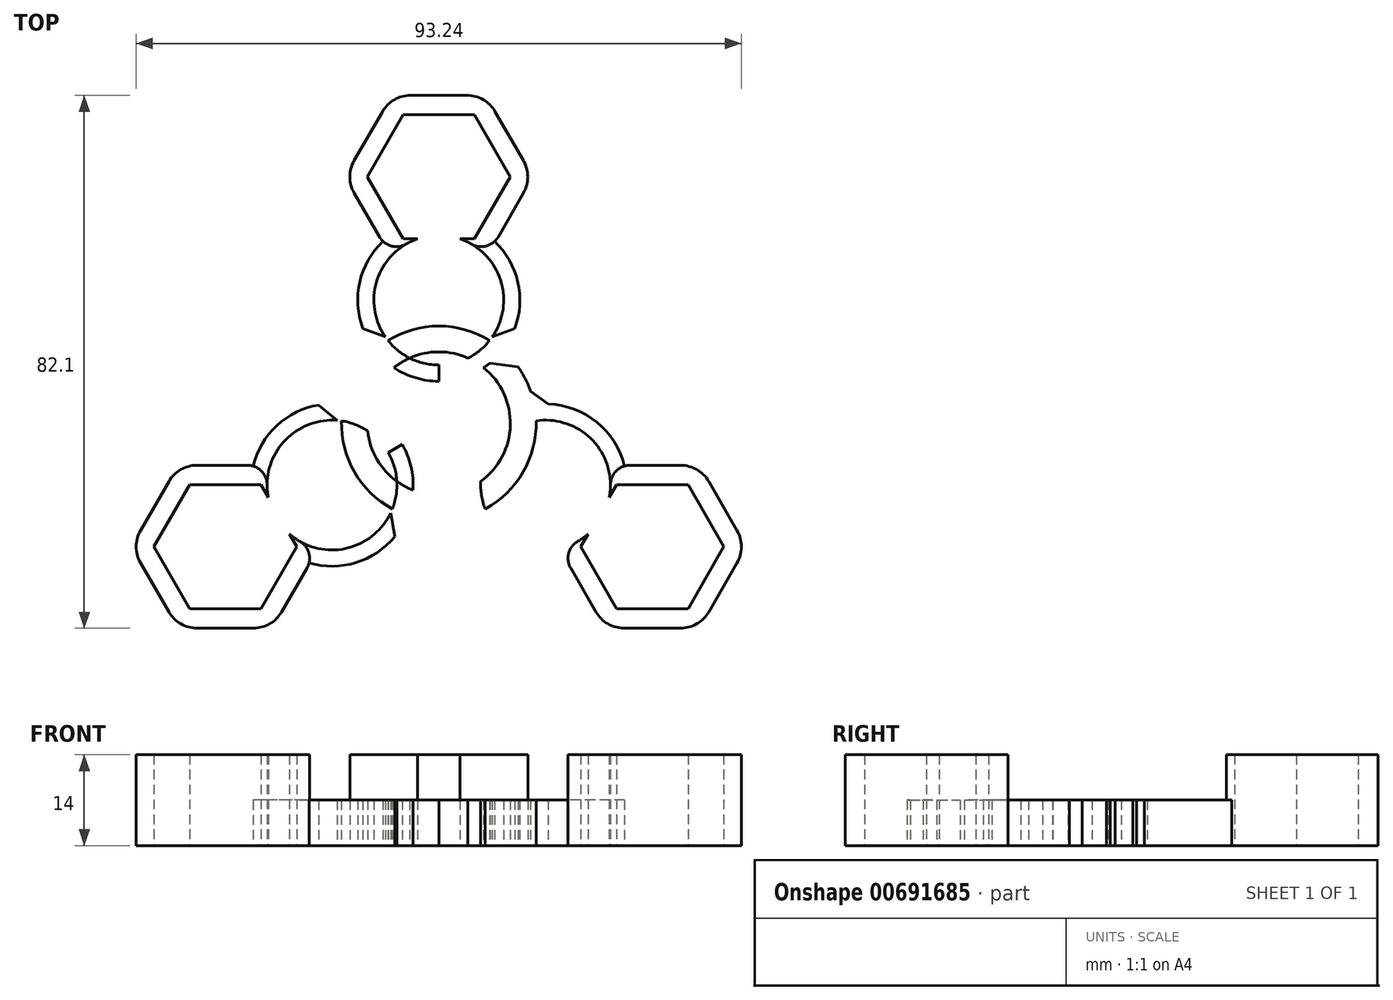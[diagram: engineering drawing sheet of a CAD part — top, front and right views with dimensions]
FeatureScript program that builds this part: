
annotation { "Feature Type Name" : "Feature", "Feature Type Description" : "" }
export const myFeature = defineFeature(function(context is Context, id is Id, definition is map)
    precondition{}
    {
        {
            var Q0;
            Q0=qCreatedBy(makeId("Top.planeOp"),FACE);
            var sketch = newSketch(context, id + "F0", { "sketchPlane" : qUnion([Q0])});
            skCircle(sketch, "E0", {"center": v(0, 0) * mm, "radius": 11.03 * mm});
            skCircle(sketch, "E1", {"center": v(0, 0) * mm, "radius": 15 * mm});
            skLineSegment(sketch, "E2", {"start": v(0, 0) * mm, "end": v(0, 38) * mm});
            skCircle(sketch, "E3.cCircle", {"center": v(0, 38) * mm, "radius": 11.03 * mm, "construction": true});
            skLineSegment(sketch, "E3.0", {"start": v(11.02, 38) * mm, "end": v(5.51, 28.45) * mm});
            skLineSegment(sketch, "E3.1", {"start": v(5.51, 28.45) * mm, "end": v(-5.51, 28.45) * mm});
            skLineSegment(sketch, "E3.2", {"start": v(-5.51, 28.45) * mm, "end": v(-11.02, 38) * mm});
            skLineSegment(sketch, "E3.3", {"start": v(-11.02, 38) * mm, "end": v(-5.51, 47.55) * mm});
            skLineSegment(sketch, "E3.4", {"start": v(-5.51, 47.55) * mm, "end": v(5.51, 47.55) * mm});
            skLineSegment(sketch, "E3.5", {"start": v(5.51, 47.55) * mm, "end": v(11.02, 38) * mm});
            skCircle(sketch, "E4", {"center": v(0, 19) * mm, "radius": 10 * mm});
            skCircle(sketch, "E5", {"center": v(0, 19) * mm, "radius": 12.5 * mm});
            skCircle(sketch, "E6.cCircle", {"center": v(0, 38) * mm, "radius": 14.49 * mm, "construction": true});
            skLineSegment(sketch, "E6.0", {"start": v(7.24, 25.45) * mm, "end": v(-7.24, 25.45) * mm});
            skLineSegment(sketch, "E6.1", {"start": v(-7.24, 25.45) * mm, "end": v(-14.49, 38) * mm});
            skLineSegment(sketch, "E6.2", {"start": v(-14.49, 38) * mm, "end": v(-7.24, 50.55) * mm});
            skLineSegment(sketch, "E6.3", {"start": v(-7.24, 50.55) * mm, "end": v(7.24, 50.55) * mm});
            skLineSegment(sketch, "E6.4", {"start": v(7.24, 50.55) * mm, "end": v(14.49, 38) * mm});
            skLineSegment(sketch, "E6.5", {"start": v(14.49, 38) * mm, "end": v(7.24, 25.45) * mm});
            skLineSegment(sketch, "E7.1.1", {"start": v(-25.66, -31.55) * mm, "end": v(-40.15, -31.55) * mm});
            skLineSegment(sketch, "E7.1.2", {"start": v(-18.42, -19) * mm, "end": v(-25.66, -31.55) * mm});
            skLineSegment(sketch, "E7.1.3", {"start": v(-47.4, -19) * mm, "end": v(-40.15, -6.45) * mm});
            skLineSegment(sketch, "E7.1.4", {"start": v(-25.66, -6.45) * mm, "end": v(-18.42, -19) * mm});
            skLineSegment(sketch, "E7.1.5", {"start": v(-40.15, -31.55) * mm, "end": v(-47.4, -19) * mm});
            skLineSegment(sketch, "E7.1.7", {"start": v(0, 0) * mm, "end": v(-32.9, -19) * mm});
            skCircle(sketch, "E7.1.8", {"center": v(-32.9, -19) * mm, "radius": 11.03 * mm, "construction": true});
            skLineSegment(sketch, "E7.1.9", {"start": v(-38.42, -9.45) * mm, "end": v(-27.4, -9.45) * mm});
            skLineSegment(sketch, "E7.1.10", {"start": v(-27.4, -9.45) * mm, "end": v(-21.88, -19) * mm});
            skLineSegment(sketch, "E7.1.11", {"start": v(-21.88, -19) * mm, "end": v(-27.4, -28.55) * mm});
            skCircle(sketch, "E7.1.12", {"center": v(-32.9, -19) * mm, "radius": 14.49 * mm, "construction": true});
            skCircle(sketch, "E7.1.13", {"center": v(-16.45, -9.5) * mm, "radius": 10 * mm});
            skLineSegment(sketch, "E7.1.14", {"start": v(-27.4, -28.55) * mm, "end": v(-38.42, -28.55) * mm});
            skLineSegment(sketch, "E7.1.15", {"start": v(-38.42, -28.55) * mm, "end": v(-43.93, -19) * mm});
            skLineSegment(sketch, "E7.1.16", {"start": v(-43.93, -19) * mm, "end": v(-38.42, -9.45) * mm});
            skCircle(sketch, "E7.1.17", {"center": v(-16.45, -9.5) * mm, "radius": 12.5 * mm});
            skLineSegment(sketch, "E7.1.18", {"start": v(-40.15, -6.45) * mm, "end": v(-25.66, -6.45) * mm});
            skLineSegment(sketch, "E7.2.1", {"start": v(40.15, -6.45) * mm, "end": v(47.4, -19) * mm});
            skLineSegment(sketch, "E7.2.2", {"start": v(25.66, -6.45) * mm, "end": v(40.15, -6.45) * mm});
            skLineSegment(sketch, "E7.2.3", {"start": v(40.15, -31.55) * mm, "end": v(25.66, -31.55) * mm});
            skLineSegment(sketch, "E7.2.4", {"start": v(18.42, -19) * mm, "end": v(25.66, -6.45) * mm});
            skLineSegment(sketch, "E7.2.5", {"start": v(47.4, -19) * mm, "end": v(40.15, -31.55) * mm});
            skLineSegment(sketch, "E7.2.7", {"start": v(0, 0) * mm, "end": v(32.9, -19) * mm});
            skCircle(sketch, "E7.2.8", {"center": v(32.9, -19) * mm, "radius": 11.03 * mm, "construction": true});
            skLineSegment(sketch, "E7.2.9", {"start": v(27.4, -28.55) * mm, "end": v(21.88, -19) * mm});
            skLineSegment(sketch, "E7.2.10", {"start": v(21.88, -19) * mm, "end": v(27.4, -9.45) * mm});
            skLineSegment(sketch, "E7.2.11", {"start": v(27.4, -9.45) * mm, "end": v(38.42, -9.45) * mm});
            skCircle(sketch, "E7.2.12", {"center": v(32.9, -19) * mm, "radius": 14.49 * mm, "construction": true});
            skCircle(sketch, "E7.2.13", {"center": v(16.45, -9.5) * mm, "radius": 10 * mm});
            skLineSegment(sketch, "E7.2.14", {"start": v(38.42, -9.45) * mm, "end": v(43.93, -19) * mm});
            skLineSegment(sketch, "E7.2.15", {"start": v(43.93, -19) * mm, "end": v(38.42, -28.55) * mm});
            skLineSegment(sketch, "E7.2.16", {"start": v(38.42, -28.55) * mm, "end": v(27.4, -28.55) * mm});
            skCircle(sketch, "E7.2.17", {"center": v(16.45, -9.5) * mm, "radius": 12.5 * mm});
            skLineSegment(sketch, "E7.2.18", {"start": v(25.66, -31.55) * mm, "end": v(18.42, -19) * mm});
            skSolve(sketch);
        }
        {
            var Q0;
            {var subQ0=sQuery(id+"F0.wireOp",EDGE,"E0");var subQ1=sQuery(id+"F0.wireOp",EDGE,"E7.1.13");var subQ2=makeQuery(id+"F0.imprint","INTERSECT",VERTEX,{"disambiguationData":[OD(1.0)],"derivedFrom":[subQ1,subQ0]});Q0=makeQuery(id+"F0.imprint","IMPRINT",FACE,{"disambiguationData":[TD([[makeQuery(id+"F0.imprint","IMPRINT",EDGE,{"disambiguationData":[TD([[subQ2,-1.0]])],"derivedFrom":subQ1}),-1.0]])]});}
            var Q1;
            {var subQ0=sQuery(id+"F0.wireOp",EDGE,"E1");var subQ1=sQuery(id+"F0.wireOp",EDGE,"E5");var subQ2=makeQuery(id+"F0.imprint","INTERSECT",VERTEX,{"disambiguationData":[OD(0.0)],"derivedFrom":[subQ1,subQ0]});Q1=makeQuery(id+"F0.imprint","IMPRINT",FACE,{"disambiguationData":[TD([[makeQuery(id+"F0.imprint","IMPRINT",EDGE,{"disambiguationData":[TD([[subQ2,-1.0]])],"derivedFrom":subQ1}),-1.0]])]});}
            var Q2;
            {var subQ0=sQuery(id+"F0.wireOp",EDGE,"E1");var subQ1=sQuery(id+"F0.wireOp",EDGE,"E4");var subQ2=makeQuery(id+"F0.imprint","INTERSECT",VERTEX,{"disambiguationData":[OD(0.0)],"derivedFrom":[subQ1,subQ0]});Q2=makeQuery(id+"F0.imprint","IMPRINT",FACE,{"disambiguationData":[TD([[makeQuery(id+"F0.imprint","IMPRINT",EDGE,{"disambiguationData":[TD([[subQ2,-1.0]])],"derivedFrom":subQ1}),-1.0]])]});}
            var Q3;
            {var subQ0=sQuery(id+"F0.wireOp",EDGE,"E0");var subQ1=sQuery(id+"F0.wireOp",EDGE,"E4");var subQ2=makeQuery(id+"F0.imprint","INTERSECT",VERTEX,{"disambiguationData":[OD(1.0)],"derivedFrom":[subQ1,subQ0]});Q3=makeQuery(id+"F0.imprint","IMPRINT",FACE,{"disambiguationData":[TD([[makeQuery(id+"F0.imprint","IMPRINT",EDGE,{"disambiguationData":[TD([[subQ2,-1.0]])],"derivedFrom":subQ1}),-1.0]])]});}
            var Q4;
            {var subQ0=sQuery(id+"F0.wireOp",EDGE,"E1");var subQ1=sQuery(id+"F0.wireOp",EDGE,"E5");var subQ2=makeQuery(id+"F0.imprint","INTERSECT",VERTEX,{"disambiguationData":[OD(1.0)],"derivedFrom":[subQ1,subQ0]});Q4=makeQuery(id+"F0.imprint","IMPRINT",FACE,{"disambiguationData":[TD([[makeQuery(id+"F0.imprint","IMPRINT",EDGE,{"disambiguationData":[TD([[subQ2,1.0]])],"derivedFrom":subQ1}),-1.0]])]});}
            var Q5;
            {var subQ0=sQuery(id+"F0.wireOp",EDGE,"E7.2.13");var subQ1=sQuery(id+"F0.wireOp",EDGE,"E0");var subQ2=makeQuery(id+"F0.imprint","INTERSECT",VERTEX,{"disambiguationData":[OD(1.0)],"derivedFrom":[subQ1,subQ0]});Q5=makeQuery(id+"F0.imprint","IMPRINT",FACE,{"disambiguationData":[TD([[makeQuery(id+"F0.imprint","IMPRINT",EDGE,{"disambiguationData":[TD([[subQ2,-1.0]])],"derivedFrom":subQ1}),-1.0]])]});}
            var Q6;
            {var subQ0=sQuery(id+"F0.wireOp",EDGE,"E7.2.17");var subQ1=sQuery(id+"F0.wireOp",EDGE,"E0");var subQ2=makeQuery(id+"F0.imprint","INTERSECT",VERTEX,{"disambiguationData":[OD(0.0)],"derivedFrom":[subQ1,subQ0]});Q6=makeQuery(id+"F0.imprint","IMPRINT",FACE,{"disambiguationData":[TD([[makeQuery(id+"F0.imprint","IMPRINT",EDGE,{"disambiguationData":[TD([[subQ2,-1.0]])],"derivedFrom":subQ1}),-1.0]])]});}
            var Q7;
            {var subQ0=sQuery(id+"F0.wireOp",EDGE,"E1");var subQ1=sQuery(id+"F0.wireOp",EDGE,"E7.1.17");var subQ2=makeQuery(id+"F0.imprint","INTERSECT",VERTEX,{"disambiguationData":[OD(0.0)],"derivedFrom":[subQ1,subQ0]});Q7=makeQuery(id+"F0.imprint","IMPRINT",FACE,{"disambiguationData":[TD([[makeQuery(id+"F0.imprint","IMPRINT",EDGE,{"disambiguationData":[TD([[subQ2,-1.0]])],"derivedFrom":subQ1}),-1.0]])]});}
            var Q8;
            {var subQ0=sQuery(id+"F0.wireOp",EDGE,"E1");var subQ1=sQuery(id+"F0.wireOp",EDGE,"E7.1.13");var subQ2=makeQuery(id+"F0.imprint","INTERSECT",VERTEX,{"disambiguationData":[OD(0.0)],"derivedFrom":[subQ1,subQ0]});Q8=makeQuery(id+"F0.imprint","IMPRINT",FACE,{"disambiguationData":[TD([[makeQuery(id+"F0.imprint","IMPRINT",EDGE,{"disambiguationData":[TD([[subQ2,-1.0]])],"derivedFrom":subQ1}),-1.0]])]});}
            var Q9;
            {var subQ0=sQuery(id+"F0.wireOp",EDGE,"E7.1.18");var subQ1=sQuery(id+"F0.wireOp",EDGE,"E7.1.13");var subQ2=makeQuery(id+"F0.imprint","INTERSECT",VERTEX,{"derivedFrom":[subQ1,subQ0]});Q9=makeQuery(id+"F0.imprint","IMPRINT",FACE,{"disambiguationData":[TD([[makeQuery(id+"F0.imprint","IMPRINT",EDGE,{"disambiguationData":[TD([[subQ2,1.0]])],"derivedFrom":subQ1}),-1.0]])]});}
            var Q10;
            {var subQ0=sQuery(id+"F0.wireOp",EDGE,"E7.1.17");var subQ1=sQuery(id+"F0.wireOp",EDGE,"E7.1.2");var subQ2=makeQuery(id+"F0.imprint","INTERSECT",VERTEX,{"derivedFrom":[subQ1,subQ0]});Q10=makeQuery(id+"F0.imprint","IMPRINT",FACE,{"disambiguationData":[TD([[makeQuery(id+"F0.imprint","IMPRINT",EDGE,{"disambiguationData":[TD([[subQ2,1.0]])],"derivedFrom":subQ1}),1.0]])]});}
            var Q11;
            {var subQ0=sQuery(id+"F0.wireOp",EDGE,"E7.2.17");var subQ1=sQuery(id+"F0.wireOp",EDGE,"E1");var subQ2=makeQuery(id+"F0.imprint","INTERSECT",VERTEX,{"disambiguationData":[OD(0.0)],"derivedFrom":[subQ1,subQ0]});Q11=makeQuery(id+"F0.imprint","IMPRINT",FACE,{"disambiguationData":[TD([[makeQuery(id+"F0.imprint","IMPRINT",EDGE,{"disambiguationData":[TD([[subQ2,-1.0]])],"derivedFrom":subQ1}),-1.0]])]});}
            var Q12;
            {var subQ0=sQuery(id+"F0.wireOp",EDGE,"E7.2.17");var subQ1=sQuery(id+"F0.wireOp",EDGE,"E7.2.2");var subQ2=makeQuery(id+"F0.imprint","INTERSECT",VERTEX,{"derivedFrom":[subQ1,subQ0]});Q12=makeQuery(id+"F0.imprint","IMPRINT",FACE,{"disambiguationData":[TD([[makeQuery(id+"F0.imprint","IMPRINT",EDGE,{"disambiguationData":[TD([[subQ2,1.0]])],"derivedFrom":subQ1}),1.0]])]});}
            var Q13;
            {var subQ0=sQuery(id+"F0.wireOp",EDGE,"E6.5");var subQ1=sQuery(id+"F0.wireOp",EDGE,"E4");var subQ2=makeQuery(id+"F0.imprint","INTERSECT",VERTEX,{"derivedFrom":[subQ1,subQ0]});Q13=makeQuery(id+"F0.imprint","IMPRINT",FACE,{"disambiguationData":[TD([[makeQuery(id+"F0.imprint","IMPRINT",EDGE,{"disambiguationData":[TD([[subQ2,1.0]])],"derivedFrom":subQ1}),-1.0]])]});}
            var Q14;
            {var subQ0=sQuery(id+"F0.wireOp",EDGE,"E6.1");var subQ1=sQuery(id+"F0.wireOp",EDGE,"E4");var subQ2=makeQuery(id+"F0.imprint","INTERSECT",VERTEX,{"derivedFrom":[subQ1,subQ0]});Q14=makeQuery(id+"F0.imprint","IMPRINT",FACE,{"disambiguationData":[TD([[makeQuery(id+"F0.imprint","IMPRINT",EDGE,{"disambiguationData":[TD([[subQ2,-1.0]])],"derivedFrom":subQ1}),-1.0]])]});}
            var Q15;
            {var subQ0=sQuery(id+"F0.wireOp",EDGE,"E0");var subQ1=sQuery(id+"F0.wireOp",EDGE,"E7.1.7");var subQ2=makeQuery(id+"F0.imprint","INTERSECT",VERTEX,{"derivedFrom":[subQ1,subQ0]});Q15=makeQuery(id+"F0.imprint","IMPRINT",FACE,{"disambiguationData":[TD([[makeQuery(id+"F0.imprint","IMPRINT",EDGE,{"disambiguationData":[TD([[subQ2,-1.0]])],"derivedFrom":subQ1}),1.0]])]});}
            var Q16;
            {var subQ0=sQuery(id+"F0.wireOp",EDGE,"E0");var subQ1=sQuery(id+"F0.wireOp",EDGE,"E7.1.7");var subQ2=makeQuery(id+"F0.imprint","INTERSECT",VERTEX,{"derivedFrom":[subQ1,subQ0]});Q16=makeQuery(id+"F0.imprint","IMPRINT",FACE,{"disambiguationData":[TD([[makeQuery(id+"F0.imprint","IMPRINT",EDGE,{"disambiguationData":[TD([[subQ2,-1.0]])],"derivedFrom":subQ1}),-1.0]])]});}
            var Q17;
            {var subQ0=sQuery(id+"F0.wireOp",EDGE,"E7.2.13");var subQ1=sQuery(id+"F0.wireOp",EDGE,"E0");var subQ2=makeQuery(id+"F0.imprint","INTERSECT",VERTEX,{"disambiguationData":[OD(0.0)],"derivedFrom":[subQ1,subQ0]});Q17=makeQuery(id+"F0.imprint","IMPRINT",FACE,{"disambiguationData":[TD([[makeQuery(id+"F0.imprint","IMPRINT",EDGE,{"disambiguationData":[TD([[subQ2,-1.0]])],"derivedFrom":subQ1}),-1.0]])]});}
            var Q18;
            {var subQ0=sQuery(id+"F0.wireOp",EDGE,"E7.2.7");var subQ1=sQuery(id+"F0.wireOp",EDGE,"E0");var subQ2=makeQuery(id+"F0.imprint","INTERSECT",VERTEX,{"derivedFrom":[subQ1,subQ0]});Q18=makeQuery(id+"F0.imprint","IMPRINT",FACE,{"disambiguationData":[TD([[makeQuery(id+"F0.imprint","IMPRINT",EDGE,{"disambiguationData":[TD([[subQ2,-1.0]])],"derivedFrom":subQ1}),-1.0]])]});}
            var Q19;
            {var subQ0=sQuery(id+"F0.wireOp",EDGE,"E0");var subQ1=sQuery(id+"F0.wireOp",EDGE,"E2");var subQ2=makeQuery(id+"F0.imprint","INTERSECT",VERTEX,{"derivedFrom":[subQ1,subQ0]});Q19=makeQuery(id+"F0.imprint","IMPRINT",FACE,{"disambiguationData":[TD([[makeQuery(id+"F0.imprint","IMPRINT",EDGE,{"disambiguationData":[TD([[subQ2,-1.0]])],"derivedFrom":subQ1}),-1.0]])]});}
            var Q20;
            {var subQ0=sQuery(id+"F0.wireOp",EDGE,"E0");var subQ1=sQuery(id+"F0.wireOp",EDGE,"E2");var subQ2=makeQuery(id+"F0.imprint","INTERSECT",VERTEX,{"derivedFrom":[subQ1,subQ0]});Q20=makeQuery(id+"F0.imprint","IMPRINT",FACE,{"disambiguationData":[TD([[makeQuery(id+"F0.imprint","IMPRINT",EDGE,{"disambiguationData":[TD([[subQ2,-1.0]])],"derivedFrom":subQ1}),1.0]])]});}
            extrude(context, id + "F1", {"entities" : qUnion([Q0, Q1, Q2, Q3, Q4, Q5, Q6, Q7, Q8, Q9, Q10, Q11, Q12, Q13, Q14, Q15, Q16, Q17, Q18, Q19, Q20]), "depth" : 7 * mm, "offsetDistance" : 25 * mm});
        }
        {
            var Q0;
            {var subQ1=sQuery(id+"F0.wireOp",EDGE,"E7.1.10");var subQ5=sQuery(id+"F0.wireOp",EDGE,"E7.1.9");var subQ6=makeQuery(id+"F0.imprint","INTERSECT",VERTEX,{"derivedFrom":[subQ5,subQ1]});Q0=makeQuery(id+"F0.imprint","IMPRINT",FACE,{"disambiguationData":[TD([[makeQuery(id+"F0.imprint","IMPRINT",EDGE,{"disambiguationData":[TD([[subQ6,1.0]])],"derivedFrom":subQ5}),1.0]])]});}
            var Q1;
            {var subQ5=sQuery(id+"F0.wireOp",EDGE,"E7.1.2");var subQ7=sQuery(id+"F0.wireOp",EDGE,"E7.1.17");var subQ9=makeQuery(id+"F0.imprint","INTERSECT",VERTEX,{"derivedFrom":[subQ5,subQ7]});Q1=makeQuery(id+"F0.imprint","IMPRINT",FACE,{"disambiguationData":[TD([[makeQuery(id+"F0.imprint","IMPRINT",EDGE,{"disambiguationData":[TD([[subQ9,1.0]])],"derivedFrom":subQ5}),-1.0]])]});}
            var Q2;
            {var subQ4=sQuery(id+"F0.wireOp",EDGE,"E7.1.1");Q2=makeQuery(id+"F0.imprint","IMPRINT",FACE,{"disambiguationData":[TD([[makeQuery(id+"F0.imprint","IMPRINT",EDGE,{"derivedFrom":subQ4}),-1.0]])]});}
            var Q3;
            {var subQ8=sQuery(id+"F0.wireOp",EDGE,"E7.2.1");Q3=makeQuery(id+"F0.imprint","IMPRINT",FACE,{"disambiguationData":[TD([[makeQuery(id+"F0.imprint","IMPRINT",EDGE,{"derivedFrom":subQ8}),-1.0]])]});}
            var Q4;
            {var subQ1=sQuery(id+"F0.wireOp",EDGE,"E7.2.10");var subQ5=sQuery(id+"F0.wireOp",EDGE,"E7.2.9");var subQ6=makeQuery(id+"F0.imprint","INTERSECT",VERTEX,{"derivedFrom":[subQ5,subQ1]});Q4=makeQuery(id+"F0.imprint","IMPRINT",FACE,{"disambiguationData":[TD([[makeQuery(id+"F0.imprint","IMPRINT",EDGE,{"disambiguationData":[TD([[subQ6,1.0]])],"derivedFrom":subQ5}),1.0]])]});}
            var Q5;
            {var subQ5=sQuery(id+"F0.wireOp",EDGE,"E7.2.2");var subQ7=sQuery(id+"F0.wireOp",EDGE,"E7.2.17");var subQ9=makeQuery(id+"F0.imprint","INTERSECT",VERTEX,{"derivedFrom":[subQ5,subQ7]});Q5=makeQuery(id+"F0.imprint","IMPRINT",FACE,{"disambiguationData":[TD([[makeQuery(id+"F0.imprint","IMPRINT",EDGE,{"disambiguationData":[TD([[subQ9,1.0]])],"derivedFrom":subQ5}),-1.0]])]});}
            var Q6;
            {var subQ11=sQuery(id+"F0.wireOp",EDGE,"E3.3");Q6=makeQuery(id+"F0.imprint","IMPRINT",FACE,{"disambiguationData":[TD([[makeQuery(id+"F0.imprint","IMPRINT",EDGE,{"derivedFrom":subQ11}),1.0]])]});}
            var Q7;
            {var subQ0=sQuery(id+"F0.wireOp",EDGE,"E3.1");var subQ1=sQuery(id+"F0.wireOp",EDGE,"E3.0");var subQ2=makeQuery(id+"F0.imprint","INTERSECT",VERTEX,{"derivedFrom":[subQ1,subQ0]});Q7=makeQuery(id+"F0.imprint","IMPRINT",FACE,{"disambiguationData":[TD([[makeQuery(id+"F0.imprint","IMPRINT",EDGE,{"disambiguationData":[TD([[subQ2,1.0]])],"derivedFrom":subQ1}),1.0]])]});}
            var Q8;
            {var subQ3=sQuery(id+"F0.wireOp",EDGE,"E3.2");var subQ6=sQuery(id+"F0.wireOp",EDGE,"E3.1");var subQ9=makeQuery(id+"F0.imprint","INTERSECT",VERTEX,{"derivedFrom":[subQ6,subQ3]});Q8=makeQuery(id+"F0.imprint","IMPRINT",FACE,{"disambiguationData":[TD([[makeQuery(id+"F0.imprint","IMPRINT",EDGE,{"disambiguationData":[TD([[subQ9,1.0]])],"derivedFrom":subQ6}),1.0]])]});}
            extrude(context, id + "F2", {"entities" : qUnion([Q0, Q1, Q2, Q3, Q4, Q5, Q6, Q7, Q8]), "operationType" : NewBodyOperationType.ADD, "depth" : 14 * mm, "offsetDistance" : 25 * mm});
        }
        {
            var Q0;
            Q0=makeQuery(id+"F1.opExtrude","SWEPT_EDGE",EDGE,{"disambiguationData":[OSD([sQuery(id+"F0.wireOp",EDGE,"E7.1.2"),sQuery(id+"F0.wireOp",EDGE,"E7.1.17")])]});
            var Q1;
            Q1=makeQuery(id+"F1.opExtrude","SWEPT_EDGE",EDGE,{"disambiguationData":[OSD([sQuery(id+"F0.wireOp",EDGE,"E7.2.17"),sQuery(id+"F0.wireOp",EDGE,"E7.2.18")])]});
            var Q2;
            Q2=makeQuery(id+"F1.opExtrude","SWEPT_EDGE",EDGE,{"disambiguationData":[OSD([sQuery(id+"F0.wireOp",EDGE,"E7.2.2"),sQuery(id+"F0.wireOp",EDGE,"E7.2.17")])]});
            var Q3;
            Q3=makeQuery(id+"F1.opExtrude","SWEPT_EDGE",EDGE,{"disambiguationData":[OSD([sQuery(id+"F0.wireOp",EDGE,"E5"),sQuery(id+"F0.wireOp",EDGE,"E6.5")])]});
            var Q4;
            Q4=makeQuery(id+"F1.opExtrude","SWEPT_EDGE",EDGE,{"disambiguationData":[OSD([sQuery(id+"F0.wireOp",EDGE,"E5"),sQuery(id+"F0.wireOp",EDGE,"E6.1")])]});
            var Q5;
            Q5=makeQuery(id+"F1.opExtrude","SWEPT_EDGE",EDGE,{"disambiguationData":[OSD([sQuery(id+"F0.wireOp",EDGE,"E7.1.17"),sQuery(id+"F0.wireOp",EDGE,"E7.1.18")])]});
            var Q6;
            {var subQ0=sQuery(id+"F0.wireOp",EDGE,"E1");var subQ1=sQuery(id+"F0.wireOp",EDGE,"E7.1.17");Q6=makeQuery(id+"F1.opExtrude","SWEPT_EDGE",EDGE,{"disambiguationData":[OSD([subQ1,subQ0]),TDD([makeQuery(id+"F0.imprint","INTERSECT",VERTEX,{"disambiguationData":[OD(1.0)],"derivedFrom":[subQ1,subQ0]})])]});}
            var Q7;
            {var subQ0=sQuery(id+"F0.wireOp",EDGE,"E1");var subQ1=sQuery(id+"F0.wireOp",EDGE,"E5");Q7=makeQuery(id+"F1.opExtrude","SWEPT_EDGE",EDGE,{"disambiguationData":[OSD([subQ1,subQ0]),TDD([makeQuery(id+"F0.imprint","INTERSECT",VERTEX,{"disambiguationData":[OD(0.0)],"derivedFrom":[subQ1,subQ0]})])]});}
            var Q8;
            {var subQ0=sQuery(id+"F0.wireOp",EDGE,"E1");var subQ1=sQuery(id+"F0.wireOp",EDGE,"E7.1.17");Q8=makeQuery(id+"F1.opExtrude","SWEPT_EDGE",EDGE,{"disambiguationData":[OSD([subQ1,subQ0]),TDD([makeQuery(id+"F0.imprint","INTERSECT",VERTEX,{"disambiguationData":[OD(0.0)],"derivedFrom":[subQ1,subQ0]})])]});}
            var Q9;
            {var subQ0=sQuery(id+"F0.wireOp",EDGE,"E7.2.17");var subQ1=sQuery(id+"F0.wireOp",EDGE,"E1");Q9=makeQuery(id+"F1.opExtrude","SWEPT_EDGE",EDGE,{"disambiguationData":[OSD([subQ1,subQ0]),TDD([makeQuery(id+"F0.imprint","INTERSECT",VERTEX,{"disambiguationData":[OD(0.0)],"derivedFrom":[subQ1,subQ0]})])]});}
            var Q10;
            {var subQ0=sQuery(id+"F0.wireOp",EDGE,"E1");var subQ1=sQuery(id+"F0.wireOp",EDGE,"E5");Q10=makeQuery(id+"F1.opExtrude","SWEPT_EDGE",EDGE,{"disambiguationData":[OSD([subQ1,subQ0]),TDD([makeQuery(id+"F0.imprint","INTERSECT",VERTEX,{"disambiguationData":[OD(1.0)],"derivedFrom":[subQ1,subQ0]})])]});}
            var Q11;
            {var subQ0=sQuery(id+"F0.wireOp",EDGE,"E7.2.17");var subQ1=sQuery(id+"F0.wireOp",EDGE,"E1");Q11=makeQuery(id+"F1.opExtrude","SWEPT_EDGE",EDGE,{"disambiguationData":[OSD([subQ1,subQ0]),TDD([makeQuery(id+"F0.imprint","INTERSECT",VERTEX,{"disambiguationData":[OD(1.0)],"derivedFrom":[subQ1,subQ0]})])]});}
            chamfer(context, id + "F3", {"entities" : qUnion([Q0, Q1, Q2, Q3, Q4, Q5, Q6, Q7, Q8, Q9, Q10, Q11]), "width" : 3 * mm, "tangentPropagation" : true});
        }
        {
            var Q0;
            Q0=makeQuery(id+"F2.opExtrude","SWEPT_EDGE",EDGE,{"disambiguationData":[OSD([sQuery(id+"F0.wireOp",EDGE,"E7.1.1"),sQuery(id+"F0.wireOp",EDGE,"E7.1.2")])]});
            var Q1;
            Q1=makeQuery(id+"F2.opExtrude","SWEPT_EDGE",EDGE,{"disambiguationData":[OSD([sQuery(id+"F0.wireOp",EDGE,"E7.1.1"),sQuery(id+"F0.wireOp",EDGE,"E7.1.5")])]});
            var Q2;
            Q2=makeQuery(id+"F2.opExtrude","SWEPT_EDGE",EDGE,{"disambiguationData":[OSD([sQuery(id+"F0.wireOp",EDGE,"E7.1.3"),sQuery(id+"F0.wireOp",EDGE,"E7.1.5")])]});
            var Q3;
            Q3=makeQuery(id+"F2.opExtrude","SWEPT_EDGE",EDGE,{"disambiguationData":[OSD([sQuery(id+"F0.wireOp",EDGE,"E7.2.3"),sQuery(id+"F0.wireOp",EDGE,"E7.2.18")])]});
            var Q4;
            Q4=makeQuery(id+"F2.opExtrude","SWEPT_EDGE",EDGE,{"disambiguationData":[OSD([sQuery(id+"F0.wireOp",EDGE,"E7.2.3"),sQuery(id+"F0.wireOp",EDGE,"E7.2.5")])]});
            var Q5;
            Q5=makeQuery(id+"F2.opExtrude","SWEPT_EDGE",EDGE,{"disambiguationData":[OSD([sQuery(id+"F0.wireOp",EDGE,"E7.2.1"),sQuery(id+"F0.wireOp",EDGE,"E7.2.5")])]});
            var Q6;
            Q6=makeQuery(id+"F2.opExtrude","SWEPT_EDGE",EDGE,{"disambiguationData":[OSD([sQuery(id+"F0.wireOp",EDGE,"E7.2.1"),sQuery(id+"F0.wireOp",EDGE,"E7.2.2")])]});
            var Q7;
            Q7=makeQuery(id+"F2.opExtrude","SWEPT_EDGE",EDGE,{"disambiguationData":[OSD([sQuery(id+"F0.wireOp",EDGE,"E7.1.3"),sQuery(id+"F0.wireOp",EDGE,"E7.1.18")])]});
            var Q8;
            Q8=makeQuery(id+"F2.opExtrude","SWEPT_EDGE",EDGE,{"disambiguationData":[OSD([sQuery(id+"F0.wireOp",EDGE,"E6.1"),sQuery(id+"F0.wireOp",EDGE,"E6.2")])]});
            var Q9;
            Q9=makeQuery(id+"F2.opExtrude","SWEPT_EDGE",EDGE,{"disambiguationData":[OSD([sQuery(id+"F0.wireOp",EDGE,"E6.2"),sQuery(id+"F0.wireOp",EDGE,"E6.3")])]});
            var Q10;
            Q10=makeQuery(id+"F2.opExtrude","SWEPT_EDGE",EDGE,{"disambiguationData":[OSD([sQuery(id+"F0.wireOp",EDGE,"E6.4"),sQuery(id+"F0.wireOp",EDGE,"E6.5")])]});
            var Q11;
            Q11=makeQuery(id+"F2.opExtrude","SWEPT_EDGE",EDGE,{"disambiguationData":[OSD([sQuery(id+"F0.wireOp",EDGE,"E6.3"),sQuery(id+"F0.wireOp",EDGE,"E6.4")])]});
            fillet(context, id + "F4", {"entities" : qUnion([Q0, Q1, Q2, Q3, Q4, Q5, Q6, Q7, Q8, Q9, Q10, Q11]), "radius" : 5 * mm, "tangentPropagation" : true, "allowEdgeOverflow" : false});
        }
        {
            var Q0;
            Q0=makeQuery(id+"F2.opExtrude","SWEPT_EDGE",EDGE,{"disambiguationData":[OSD([sQuery(id+"F0.wireOp",EDGE,"E7.1.2"),sQuery(id+"F0.wireOp",EDGE,"E7.1.13")])]});
            var Q1;
            Q1=makeQuery(id+"F2.opExtrude","SWEPT_EDGE",EDGE,{"disambiguationData":[OSD([sQuery(id+"F0.wireOp",EDGE,"E7.1.13"),sQuery(id+"F0.wireOp",EDGE,"E7.1.18")])]});
            var Q2;
            Q2=makeQuery(id+"F2.opExtrude","SWEPT_EDGE",EDGE,{"disambiguationData":[OSD([sQuery(id+"F0.wireOp",EDGE,"E7.2.13"),sQuery(id+"F0.wireOp",EDGE,"E7.2.18")])]});
            var Q3;
            Q3=makeQuery(id+"F2.opExtrude","SWEPT_EDGE",EDGE,{"disambiguationData":[OSD([sQuery(id+"F0.wireOp",EDGE,"E7.2.2"),sQuery(id+"F0.wireOp",EDGE,"E7.2.13")])]});
            var Q4;
            Q4=makeQuery(id+"F2.opExtrude","SWEPT_EDGE",EDGE,{"disambiguationData":[OSD([sQuery(id+"F0.wireOp",EDGE,"E4"),sQuery(id+"F0.wireOp",EDGE,"E6.5")])]});
            var Q5;
            Q5=makeQuery(id+"F2.opExtrude","SWEPT_EDGE",EDGE,{"disambiguationData":[OSD([sQuery(id+"F0.wireOp",EDGE,"E4"),sQuery(id+"F0.wireOp",EDGE,"E6.1")])]});
            fillet(context, id + "F5", {"entities" : qUnion([Q0, Q1, Q2, Q3, Q4, Q5]), "radius" : 3 * mm, "tangentPropagation" : true, "allowEdgeOverflow" : false});
        }
    });
